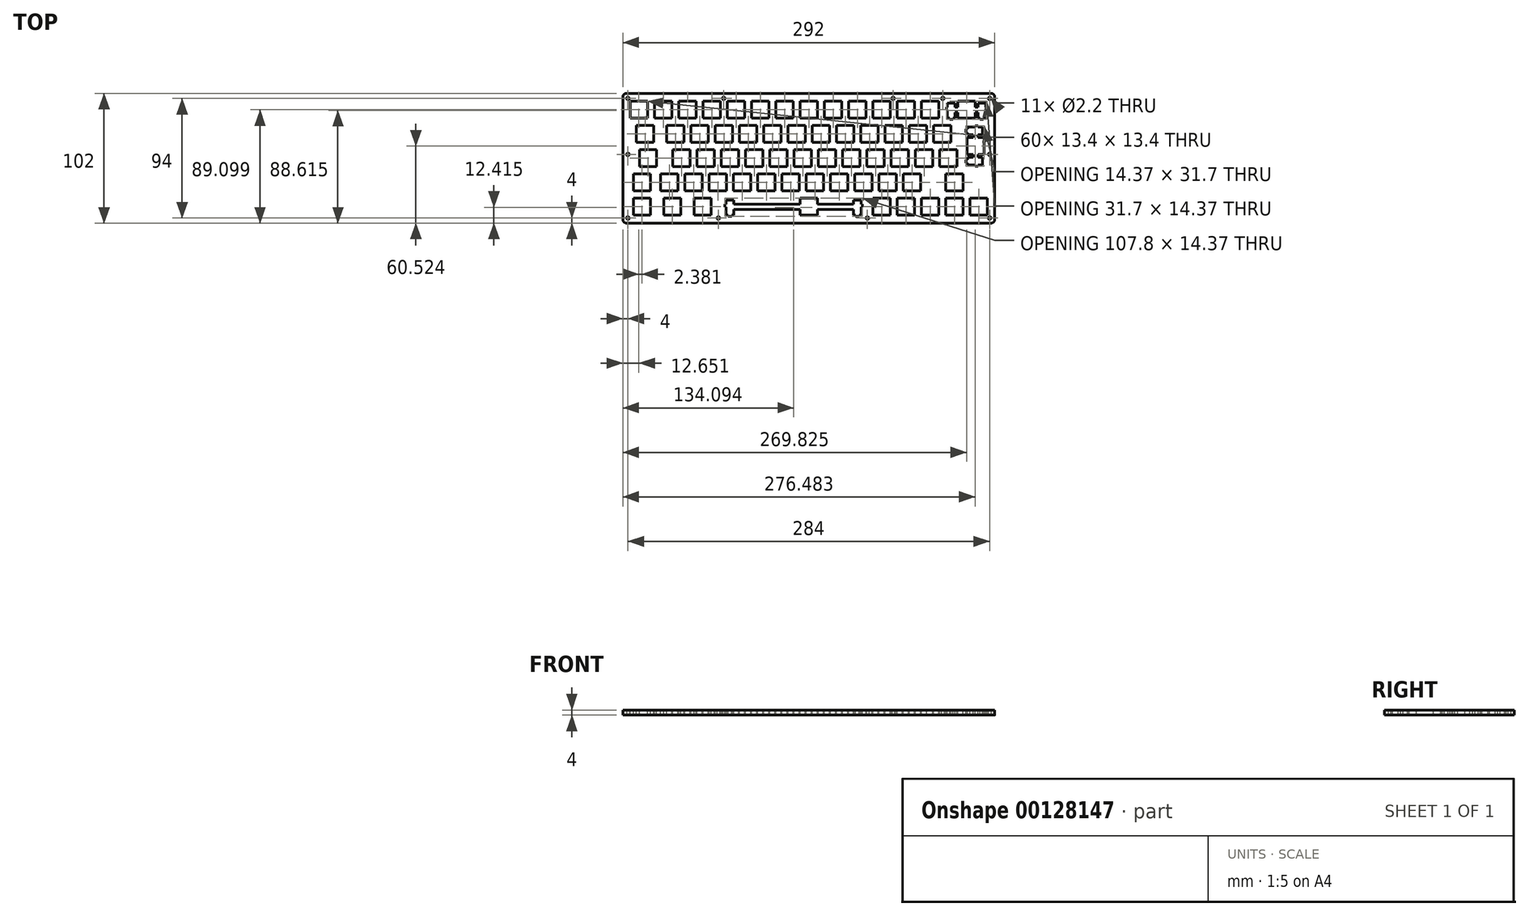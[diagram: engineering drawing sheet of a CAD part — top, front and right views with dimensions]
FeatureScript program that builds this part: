
annotation { "Feature Type Name" : "Feature", "Feature Type Description" : "" }
export const myFeature = defineFeature(function(context is Context, id is Id, definition is map)
    precondition{}
    {
        {
            var Q0;
            Q0=qCreatedBy(makeId("Top.planeOp"),FACE);
            var sketch = newSketch(context, id + "F0", { "sketchPlane" : qUnion([Q0])});
            skLineSegment(sketch, "E0.bottom", {"start": v(-143, 51) * mm, "end": v(143, 51) * mm});
            skLineSegment(sketch, "E0.top", {"start": v(-143, -51) * mm, "end": v(143, -51) * mm});
            skLineSegment(sketch, "E0.left", {"start": v(-146, 48) * mm, "end": v(-146, -48) * mm});
            skLineSegment(sketch, "E0.right", {"start": v(146, 48) * mm, "end": v(146, -48) * mm});
            skPoint(sketch, "E0.middle", {"position": v(0, 0) * mm});
            skPoint(sketch, "E1.visualSharp", {"position": v(-146, 51) * mm});
            skArc(sketch, "E1.filletArc", {"start": v(-143, 51) * mm, "mid": v(-145.12, 50.12) * mm, "end": v(-146, 48) * mm});
            skPoint(sketch, "E2.visualSharp", {"position": v(-146, -51) * mm});
            skArc(sketch, "E2.filletArc", {"start": v(-146, -48) * mm, "mid": v(-145.12, -50.12) * mm, "end": v(-143, -51) * mm});
            skPoint(sketch, "E3.visualSharp", {"position": v(146, 51) * mm});
            skArc(sketch, "E3.filletArc", {"start": v(146, 48) * mm, "mid": v(145.12, 50.12) * mm, "end": v(143, 51) * mm});
            skPoint(sketch, "E4.visualSharp", {"position": v(146, -51) * mm});
            skArc(sketch, "E4.filletArc", {"start": v(143, -51) * mm, "mid": v(145.12, -50.12) * mm, "end": v(146, -48) * mm});
            skCircle(sketch, "E5", {"center": v(-142, 47) * mm, "radius": 1.1 * mm});
            skCircle(sketch, "E6", {"center": v(-66.83, 47) * mm, "radius": 1.1 * mm});
            skCircle(sketch, "E7", {"center": v(66.17, 47) * mm, "radius": 1.1 * mm});
            skCircle(sketch, "E8", {"center": v(105.17, 47) * mm, "radius": 1.1 * mm});
            skCircle(sketch, "E9", {"center": v(142, 47) * mm, "radius": 1.1 * mm});
            skCircle(sketch, "E10", {"center": v(-142, -47) * mm, "radius": 1.1 * mm});
            skCircle(sketch, "E11", {"center": v(142, -47) * mm, "radius": 1.1 * mm});
            skCircle(sketch, "E12", {"center": v(-71, -47) * mm, "radius": 1.1 * mm});
            skCircle(sketch, "E13", {"center": v(46, -47) * mm, "radius": 1.1 * mm});
            skCircle(sketch, "E14", {"center": v(-142, 3) * mm, "radius": 1.1 * mm});
            skCircle(sketch, "E15", {"center": v(142, 3) * mm, "radius": 1.1 * mm});
            skSolve(sketch);
        }
        {
            var Q0;
            Q0=qSketchRegion(id+"F0",true);
            extrude(context, id + "F1", {"entities" : qUnion([Q0]), "depth" : 4 * mm});
        }
        {
            var Q0;
            Q0=makeQuery(id+"F1.opExtrude","CAP_FACE",FACE,{"disambiguationData":[OSD([sQuery(id+"F0.wireOp",EDGE,"E0.bottom"),sQuery(id+"F0.wireOp",EDGE,"E0.top"),sQuery(id+"F0.wireOp",EDGE,"E0.left"),sQuery(id+"F0.wireOp",EDGE,"E0.right"),sQuery(id+"F0.wireOp",EDGE,"E1.filletArc"),sQuery(id+"F0.wireOp",EDGE,"E2.filletArc"),sQuery(id+"F0.wireOp",EDGE,"E3.filletArc"),sQuery(id+"F0.wireOp",EDGE,"E4.filletArc"),sQuery(id+"F0.wireOp",EDGE,"E5"),sQuery(id+"F0.wireOp",EDGE,"E6"),sQuery(id+"F0.wireOp",EDGE,"E7"),sQuery(id+"F0.wireOp",EDGE,"E8"),sQuery(id+"F0.wireOp",EDGE,"E9"),sQuery(id+"F0.wireOp",EDGE,"E10"),sQuery(id+"F0.wireOp",EDGE,"E11"),sQuery(id+"F0.wireOp",EDGE,"E12"),sQuery(id+"F0.wireOp",EDGE,"E13"),sQuery(id+"F0.wireOp",EDGE,"E14"),sQuery(id+"F0.wireOp",EDGE,"E15")])],"isStart":false});
            var sketch = newSketch(context, id + "F2", { "sketchPlane" : qUnion([Q0])});
            skLineSegment(sketch, "E16", {"start": v(-18.6, -36.1) * mm, "end": v(-58.88, -36.1) * mm});
            skLineSegment(sketch, "E17", {"start": v(-58.88, -36.1) * mm, "end": v(-58.88, -32.87) * mm});
            skLineSegment(sketch, "E18", {"start": v(-58.88, -32.87) * mm, "end": v(-64.93, -32.87) * mm});
            skLineSegment(sketch, "E19", {"start": v(-64.93, -32.87) * mm, "end": v(-64.93, -36.1) * mm});
            skLineSegment(sketch, "E20", {"start": v(-64.93, -36.1) * mm, "end": v(-65.8, -36.1) * mm});
            skLineSegment(sketch, "E21", {"start": v(-65.8, -36.1) * mm, "end": v(-65.8, -38.3) * mm});
            skLineSegment(sketch, "E22", {"start": v(-65.8, -38.3) * mm, "end": v(-64.93, -38.3) * mm});
            skLineSegment(sketch, "E23", {"start": v(-64.93, -38.3) * mm, "end": v(-64.93, -44.57) * mm});
            skLineSegment(sketch, "E24", {"start": v(-64.93, -44.57) * mm, "end": v(-63.26, -44.57) * mm});
            skLineSegment(sketch, "E25", {"start": v(-63.26, -44.57) * mm, "end": v(-63.26, -45.77) * mm});
            skLineSegment(sketch, "E26", {"start": v(-63.26, -45.77) * mm, "end": v(-60.56, -45.77) * mm});
            skLineSegment(sketch, "E27", {"start": v(-60.56, -45.77) * mm, "end": v(-60.56, -44.57) * mm});
            skLineSegment(sketch, "E28", {"start": v(-60.56, -44.57) * mm, "end": v(-58.88, -44.57) * mm});
            skLineSegment(sketch, "E29", {"start": v(-58.88, -44.57) * mm, "end": v(-58.88, -40.1) * mm});
            skLineSegment(sketch, "E30", {"start": v(-58.88, -40.1) * mm, "end": v(-18.6, -40.1) * mm});
            skLineSegment(sketch, "E31", {"start": v(6.7, -40.1) * mm, "end": v(35.07, -40.1) * mm});
            skLineSegment(sketch, "E32", {"start": v(35.07, -40.1) * mm, "end": v(35.07, -44.57) * mm});
            skLineSegment(sketch, "E33", {"start": v(35.07, -44.57) * mm, "end": v(36.74, -44.57) * mm});
            skLineSegment(sketch, "E34", {"start": v(36.74, -44.57) * mm, "end": v(36.74, -45.77) * mm});
            skLineSegment(sketch, "E35", {"start": v(36.74, -45.77) * mm, "end": v(39.44, -45.77) * mm});
            skLineSegment(sketch, "E36", {"start": v(39.44, -45.77) * mm, "end": v(39.44, -44.57) * mm});
            skLineSegment(sketch, "E37", {"start": v(39.44, -44.57) * mm, "end": v(41.12, -44.57) * mm});
            skLineSegment(sketch, "E38", {"start": v(41.12, -44.57) * mm, "end": v(41.12, -38.3) * mm});
            skLineSegment(sketch, "E39", {"start": v(41.12, -38.3) * mm, "end": v(42, -38.3) * mm});
            skLineSegment(sketch, "E40", {"start": v(42, -38.3) * mm, "end": v(42, -36.1) * mm});
            skLineSegment(sketch, "E41", {"start": v(42, -36.1) * mm, "end": v(41.12, -36.1) * mm});
            skLineSegment(sketch, "E42", {"start": v(41.12, -36.1) * mm, "end": v(41.12, -32.87) * mm});
            skLineSegment(sketch, "E43", {"start": v(41.12, -32.87) * mm, "end": v(35.07, -32.87) * mm});
            skLineSegment(sketch, "E44", {"start": v(35.07, -32.87) * mm, "end": v(35.07, -36.1) * mm});
            skLineSegment(sketch, "E45", {"start": v(35.07, -36.1) * mm, "end": v(6.7, -36.1) * mm});
            skLineSegment(sketch, "E46", {"start": v(-137.67, -31.4) * mm, "end": v(-124.27, -31.4) * mm});
            skLineSegment(sketch, "E47", {"start": v(-124.27, -31.4) * mm, "end": v(-124.27, -44.8) * mm});
            skLineSegment(sketch, "E48", {"start": v(-124.27, -44.8) * mm, "end": v(-137.67, -44.8) * mm});
            skLineSegment(sketch, "E49", {"start": v(-137.67, -44.8) * mm, "end": v(-137.67, -31.4) * mm});
            skLineSegment(sketch, "E50", {"start": v(-113.86, -31.4) * mm, "end": v(-100.46, -31.4) * mm});
            skLineSegment(sketch, "E51", {"start": v(-100.46, -31.4) * mm, "end": v(-100.46, -44.8) * mm});
            skLineSegment(sketch, "E52", {"start": v(-100.46, -44.8) * mm, "end": v(-113.86, -44.8) * mm});
            skLineSegment(sketch, "E53", {"start": v(-113.86, -44.8) * mm, "end": v(-113.86, -31.4) * mm});
            skLineSegment(sketch, "E54", {"start": v(-90.04, -31.4) * mm, "end": v(-76.64, -31.4) * mm});
            skLineSegment(sketch, "E55", {"start": v(-76.64, -31.4) * mm, "end": v(-76.64, -44.8) * mm});
            skLineSegment(sketch, "E56", {"start": v(-76.64, -44.8) * mm, "end": v(-90.04, -44.8) * mm});
            skLineSegment(sketch, "E57", {"start": v(-90.04, -44.8) * mm, "end": v(-90.04, -31.4) * mm});
            skLineSegment(sketch, "E58", {"start": v(50.45, -31.4) * mm, "end": v(63.85, -31.4) * mm});
            skLineSegment(sketch, "E59", {"start": v(63.85, -31.4) * mm, "end": v(63.85, -44.8) * mm});
            skLineSegment(sketch, "E60", {"start": v(63.85, -44.8) * mm, "end": v(50.45, -44.8) * mm});
            skLineSegment(sketch, "E61", {"start": v(50.45, -44.8) * mm, "end": v(50.45, -31.4) * mm});
            skLineSegment(sketch, "E62", {"start": v(69.5, -31.4) * mm, "end": v(82.9, -31.4) * mm});
            skLineSegment(sketch, "E63", {"start": v(82.9, -31.4) * mm, "end": v(82.9, -44.8) * mm});
            skLineSegment(sketch, "E64", {"start": v(82.9, -44.8) * mm, "end": v(69.5, -44.8) * mm});
            skLineSegment(sketch, "E65", {"start": v(69.5, -44.8) * mm, "end": v(69.5, -31.4) * mm});
            skLineSegment(sketch, "E66", {"start": v(88.55, -31.4) * mm, "end": v(101.95, -31.4) * mm});
            skLineSegment(sketch, "E67", {"start": v(101.95, -31.4) * mm, "end": v(101.95, -44.8) * mm});
            skLineSegment(sketch, "E68", {"start": v(101.95, -44.8) * mm, "end": v(88.55, -44.8) * mm});
            skLineSegment(sketch, "E69", {"start": v(88.55, -44.8) * mm, "end": v(88.55, -31.4) * mm});
            skLineSegment(sketch, "E70", {"start": v(107.6, -31.4) * mm, "end": v(121, -31.4) * mm});
            skLineSegment(sketch, "E71", {"start": v(121, -31.4) * mm, "end": v(121, -44.8) * mm});
            skLineSegment(sketch, "E72", {"start": v(121, -44.8) * mm, "end": v(107.6, -44.8) * mm});
            skLineSegment(sketch, "E73", {"start": v(107.6, -44.8) * mm, "end": v(107.6, -31.4) * mm});
            skLineSegment(sketch, "E74", {"start": v(126.65, -31.4) * mm, "end": v(140.05, -31.4) * mm});
            skLineSegment(sketch, "E75", {"start": v(140.05, -31.4) * mm, "end": v(140.05, -44.8) * mm});
            skLineSegment(sketch, "E76", {"start": v(140.05, -44.8) * mm, "end": v(126.65, -44.8) * mm});
            skLineSegment(sketch, "E77", {"start": v(126.65, -44.8) * mm, "end": v(126.65, -31.4) * mm});
            skLineSegment(sketch, "E78", {"start": v(-137.67, -12.35) * mm, "end": v(-124.27, -12.35) * mm});
            skLineSegment(sketch, "E79", {"start": v(-124.27, -12.35) * mm, "end": v(-124.27, -25.75) * mm});
            skLineSegment(sketch, "E80", {"start": v(-124.27, -25.75) * mm, "end": v(-137.67, -25.75) * mm});
            skLineSegment(sketch, "E81", {"start": v(-137.67, -25.75) * mm, "end": v(-137.67, -12.35) * mm});
            skLineSegment(sketch, "E82", {"start": v(-116.24, -12.35) * mm, "end": v(-102.84, -12.35) * mm});
            skLineSegment(sketch, "E83", {"start": v(-102.84, -12.35) * mm, "end": v(-102.84, -25.75) * mm});
            skLineSegment(sketch, "E84", {"start": v(-102.84, -25.75) * mm, "end": v(-116.24, -25.75) * mm});
            skLineSegment(sketch, "E85", {"start": v(-116.24, -25.75) * mm, "end": v(-116.24, -12.35) * mm});
            skLineSegment(sketch, "E86", {"start": v(-97.19, -12.35) * mm, "end": v(-83.79, -12.35) * mm});
            skLineSegment(sketch, "E87", {"start": v(-83.79, -12.35) * mm, "end": v(-83.79, -25.75) * mm});
            skLineSegment(sketch, "E88", {"start": v(-83.79, -25.75) * mm, "end": v(-97.19, -25.75) * mm});
            skLineSegment(sketch, "E89", {"start": v(-97.19, -25.75) * mm, "end": v(-97.19, -12.35) * mm});
            skLineSegment(sketch, "E90", {"start": v(-78.14, -12.35) * mm, "end": v(-64.74, -12.35) * mm});
            skLineSegment(sketch, "E91", {"start": v(-64.74, -12.35) * mm, "end": v(-64.74, -25.75) * mm});
            skLineSegment(sketch, "E92", {"start": v(-64.74, -25.75) * mm, "end": v(-78.14, -25.75) * mm});
            skLineSegment(sketch, "E93", {"start": v(-78.14, -25.75) * mm, "end": v(-78.14, -12.35) * mm});
            skLineSegment(sketch, "E94", {"start": v(-59.09, -12.35) * mm, "end": v(-45.69, -12.35) * mm});
            skLineSegment(sketch, "E95", {"start": v(-45.69, -12.35) * mm, "end": v(-45.69, -25.75) * mm});
            skLineSegment(sketch, "E96", {"start": v(-45.69, -25.75) * mm, "end": v(-59.09, -25.75) * mm});
            skLineSegment(sketch, "E97", {"start": v(-59.09, -25.75) * mm, "end": v(-59.09, -12.35) * mm});
            skLineSegment(sketch, "E98", {"start": v(-40.04, -12.35) * mm, "end": v(-26.64, -12.35) * mm});
            skLineSegment(sketch, "E99", {"start": v(-26.64, -12.35) * mm, "end": v(-26.64, -25.75) * mm});
            skLineSegment(sketch, "E100", {"start": v(-26.64, -25.75) * mm, "end": v(-40.04, -25.75) * mm});
            skLineSegment(sketch, "E101", {"start": v(-40.04, -25.75) * mm, "end": v(-40.04, -12.35) * mm});
            skLineSegment(sketch, "E102", {"start": v(-20.99, -12.35) * mm, "end": v(-7.59, -12.35) * mm});
            skLineSegment(sketch, "E103", {"start": v(-7.59, -12.35) * mm, "end": v(-7.59, -25.75) * mm});
            skLineSegment(sketch, "E104", {"start": v(-7.59, -25.75) * mm, "end": v(-20.99, -25.75) * mm});
            skLineSegment(sketch, "E105", {"start": v(-20.99, -25.75) * mm, "end": v(-20.99, -12.35) * mm});
            skLineSegment(sketch, "E106", {"start": v(-1.94, -12.35) * mm, "end": v(11.46, -12.35) * mm});
            skLineSegment(sketch, "E107", {"start": v(11.46, -12.35) * mm, "end": v(11.46, -25.75) * mm});
            skLineSegment(sketch, "E108", {"start": v(11.46, -25.75) * mm, "end": v(-1.94, -25.75) * mm});
            skLineSegment(sketch, "E109", {"start": v(-1.94, -25.75) * mm, "end": v(-1.94, -12.35) * mm});
            skLineSegment(sketch, "E110", {"start": v(17.11, -12.35) * mm, "end": v(30.51, -12.35) * mm});
            skLineSegment(sketch, "E111", {"start": v(30.51, -12.35) * mm, "end": v(30.51, -25.75) * mm});
            skLineSegment(sketch, "E112", {"start": v(30.51, -25.75) * mm, "end": v(17.11, -25.75) * mm});
            skLineSegment(sketch, "E113", {"start": v(17.11, -25.75) * mm, "end": v(17.11, -12.35) * mm});
            skLineSegment(sketch, "E114", {"start": v(36.16, -12.35) * mm, "end": v(49.56, -12.35) * mm});
            skLineSegment(sketch, "E115", {"start": v(49.56, -12.35) * mm, "end": v(49.56, -25.75) * mm});
            skLineSegment(sketch, "E116", {"start": v(49.56, -25.75) * mm, "end": v(36.16, -25.75) * mm});
            skLineSegment(sketch, "E117", {"start": v(36.16, -25.75) * mm, "end": v(36.16, -12.35) * mm});
            skLineSegment(sketch, "E118", {"start": v(55.21, -12.35) * mm, "end": v(68.61, -12.35) * mm});
            skLineSegment(sketch, "E119", {"start": v(68.61, -12.35) * mm, "end": v(68.61, -25.75) * mm});
            skLineSegment(sketch, "E120", {"start": v(68.61, -25.75) * mm, "end": v(55.21, -25.75) * mm});
            skLineSegment(sketch, "E121", {"start": v(55.21, -25.75) * mm, "end": v(55.21, -12.35) * mm});
            skLineSegment(sketch, "E122", {"start": v(74.26, -12.35) * mm, "end": v(87.66, -12.35) * mm});
            skLineSegment(sketch, "E123", {"start": v(87.66, -12.35) * mm, "end": v(87.66, -25.75) * mm});
            skLineSegment(sketch, "E124", {"start": v(87.66, -25.75) * mm, "end": v(74.26, -25.75) * mm});
            skLineSegment(sketch, "E125", {"start": v(74.26, -25.75) * mm, "end": v(74.26, -12.35) * mm});
            skLineSegment(sketch, "E126", {"start": v(107.6, -12.35) * mm, "end": v(121, -12.35) * mm});
            skLineSegment(sketch, "E127", {"start": v(121, -12.35) * mm, "end": v(121, -25.75) * mm});
            skLineSegment(sketch, "E128", {"start": v(121, -25.75) * mm, "end": v(107.6, -25.75) * mm});
            skLineSegment(sketch, "E129", {"start": v(107.6, -25.75) * mm, "end": v(107.6, -12.35) * mm});
            skLineSegment(sketch, "E130", {"start": v(-132.9, 6.7) * mm, "end": v(-119.5, 6.7) * mm});
            skLineSegment(sketch, "E131", {"start": v(-119.5, 6.7) * mm, "end": v(-119.5, -6.7) * mm});
            skLineSegment(sketch, "E132", {"start": v(-119.5, -6.7) * mm, "end": v(-132.9, -6.7) * mm});
            skLineSegment(sketch, "E133", {"start": v(-132.9, -6.7) * mm, "end": v(-132.9, 6.7) * mm});
            skLineSegment(sketch, "E134", {"start": v(-106.71, 6.7) * mm, "end": v(-93.31, 6.7) * mm});
            skLineSegment(sketch, "E135", {"start": v(-93.31, 6.7) * mm, "end": v(-93.31, -6.7) * mm});
            skLineSegment(sketch, "E136", {"start": v(-93.31, -6.7) * mm, "end": v(-106.71, -6.7) * mm});
            skLineSegment(sketch, "E137", {"start": v(-106.71, -6.7) * mm, "end": v(-106.71, 6.7) * mm});
            skLineSegment(sketch, "E138", {"start": v(-87.66, 6.7) * mm, "end": v(-74.26, 6.7) * mm});
            skLineSegment(sketch, "E139", {"start": v(-74.26, 6.7) * mm, "end": v(-74.26, -6.7) * mm});
            skLineSegment(sketch, "E140", {"start": v(-74.26, -6.7) * mm, "end": v(-87.66, -6.7) * mm});
            skLineSegment(sketch, "E141", {"start": v(-87.66, -6.7) * mm, "end": v(-87.66, 6.7) * mm});
            skLineSegment(sketch, "E142", {"start": v(-68.61, 6.7) * mm, "end": v(-55.21, 6.7) * mm});
            skLineSegment(sketch, "E143", {"start": v(-55.21, 6.7) * mm, "end": v(-55.21, -6.7) * mm});
            skLineSegment(sketch, "E144", {"start": v(-55.21, -6.7) * mm, "end": v(-68.61, -6.7) * mm});
            skLineSegment(sketch, "E145", {"start": v(-68.61, -6.7) * mm, "end": v(-68.61, 6.7) * mm});
            skLineSegment(sketch, "E146", {"start": v(-49.56, 6.7) * mm, "end": v(-36.16, 6.7) * mm});
            skLineSegment(sketch, "E147", {"start": v(-36.16, 6.7) * mm, "end": v(-36.16, -6.7) * mm});
            skLineSegment(sketch, "E148", {"start": v(-36.16, -6.7) * mm, "end": v(-49.56, -6.7) * mm});
            skLineSegment(sketch, "E149", {"start": v(-49.56, -6.7) * mm, "end": v(-49.56, 6.7) * mm});
            skLineSegment(sketch, "E150", {"start": v(-30.51, 6.7) * mm, "end": v(-17.11, 6.7) * mm});
            skLineSegment(sketch, "E151", {"start": v(-17.11, 6.7) * mm, "end": v(-17.11, -6.7) * mm});
            skLineSegment(sketch, "E152", {"start": v(-17.11, -6.7) * mm, "end": v(-30.51, -6.7) * mm});
            skLineSegment(sketch, "E153", {"start": v(-30.51, -6.7) * mm, "end": v(-30.51, 6.7) * mm});
            skLineSegment(sketch, "E154", {"start": v(-11.46, 6.7) * mm, "end": v(1.94, 6.7) * mm});
            skLineSegment(sketch, "E155", {"start": v(1.94, 6.7) * mm, "end": v(1.94, -6.7) * mm});
            skLineSegment(sketch, "E156", {"start": v(1.94, -6.7) * mm, "end": v(-11.46, -6.7) * mm});
            skLineSegment(sketch, "E157", {"start": v(-11.46, -6.7) * mm, "end": v(-11.46, 6.7) * mm});
            skLineSegment(sketch, "E158", {"start": v(7.59, 6.7) * mm, "end": v(20.99, 6.7) * mm});
            skLineSegment(sketch, "E159", {"start": v(20.99, 6.7) * mm, "end": v(20.99, -6.7) * mm});
            skLineSegment(sketch, "E160", {"start": v(20.99, -6.7) * mm, "end": v(7.59, -6.7) * mm});
            skLineSegment(sketch, "E161", {"start": v(7.59, -6.7) * mm, "end": v(7.59, 6.7) * mm});
            skLineSegment(sketch, "E162", {"start": v(26.64, 6.7) * mm, "end": v(40.04, 6.7) * mm});
            skLineSegment(sketch, "E163", {"start": v(40.04, 6.7) * mm, "end": v(40.04, -6.7) * mm});
            skLineSegment(sketch, "E164", {"start": v(40.04, -6.7) * mm, "end": v(26.64, -6.7) * mm});
            skLineSegment(sketch, "E165", {"start": v(26.64, -6.7) * mm, "end": v(26.64, 6.7) * mm});
            skLineSegment(sketch, "E166", {"start": v(45.69, 6.7) * mm, "end": v(59.09, 6.7) * mm});
            skLineSegment(sketch, "E167", {"start": v(59.09, 6.7) * mm, "end": v(59.09, -6.7) * mm});
            skLineSegment(sketch, "E168", {"start": v(59.09, -6.7) * mm, "end": v(45.69, -6.7) * mm});
            skLineSegment(sketch, "E169", {"start": v(45.69, -6.7) * mm, "end": v(45.69, 6.7) * mm});
            skLineSegment(sketch, "E170", {"start": v(64.74, 6.7) * mm, "end": v(78.14, 6.7) * mm});
            skLineSegment(sketch, "E171", {"start": v(78.14, 6.7) * mm, "end": v(78.14, -6.7) * mm});
            skLineSegment(sketch, "E172", {"start": v(78.14, -6.7) * mm, "end": v(64.74, -6.7) * mm});
            skLineSegment(sketch, "E173", {"start": v(64.74, -6.7) * mm, "end": v(64.74, 6.7) * mm});
            skLineSegment(sketch, "E174", {"start": v(83.79, 6.7) * mm, "end": v(97.19, 6.7) * mm});
            skLineSegment(sketch, "E175", {"start": v(97.19, 6.7) * mm, "end": v(97.19, -6.7) * mm});
            skLineSegment(sketch, "E176", {"start": v(97.19, -6.7) * mm, "end": v(83.79, -6.7) * mm});
            skLineSegment(sketch, "E177", {"start": v(83.79, -6.7) * mm, "end": v(83.79, 6.7) * mm});
            skLineSegment(sketch, "E178", {"start": v(102.84, 6.7) * mm, "end": v(116.24, 6.7) * mm});
            skLineSegment(sketch, "E179", {"start": v(116.24, 6.7) * mm, "end": v(116.24, -6.7) * mm});
            skLineSegment(sketch, "E180", {"start": v(116.24, -6.7) * mm, "end": v(102.84, -6.7) * mm});
            skLineSegment(sketch, "E181", {"start": v(102.84, -6.7) * mm, "end": v(102.84, 6.7) * mm});
            skLineSegment(sketch, "E182", {"start": v(130.77, 25.37) * mm, "end": v(130.77, 24.5) * mm});
            skLineSegment(sketch, "E183", {"start": v(130.77, 24.5) * mm, "end": v(124.5, 24.5) * mm});
            skLineSegment(sketch, "E184", {"start": v(124.5, 24.5) * mm, "end": v(124.5, 22.83) * mm});
            skLineSegment(sketch, "E185", {"start": v(124.5, 22.83) * mm, "end": v(123.3, 22.83) * mm});
            skLineSegment(sketch, "E186", {"start": v(123.3, 22.83) * mm, "end": v(123.3, 20.12) * mm});
            skLineSegment(sketch, "E187", {"start": v(123.3, 20.12) * mm, "end": v(124.5, 20.12) * mm});
            skLineSegment(sketch, "E188", {"start": v(124.5, 20.12) * mm, "end": v(124.5, 18.45) * mm});
            skLineSegment(sketch, "E189", {"start": v(124.5, 18.45) * mm, "end": v(128.97, 18.45) * mm});
            skLineSegment(sketch, "E190", {"start": v(128.97, 18.45) * mm, "end": v(128.97, 16.23) * mm});
            skLineSegment(sketch, "E191", {"start": v(128.97, 16.23) * mm, "end": v(124.27, 16.23) * mm});
            skLineSegment(sketch, "E192", {"start": v(124.27, 16.23) * mm, "end": v(124.27, 2.82) * mm});
            skLineSegment(sketch, "E193", {"start": v(124.27, 2.82) * mm, "end": v(128.97, 2.82) * mm});
            skLineSegment(sketch, "E194", {"start": v(128.97, 2.82) * mm, "end": v(128.97, 0.6) * mm});
            skLineSegment(sketch, "E195", {"start": v(128.97, 0.6) * mm, "end": v(124.5, 0.6) * mm});
            skLineSegment(sketch, "E196", {"start": v(124.5, 0.6) * mm, "end": v(124.5, -1.08) * mm});
            skLineSegment(sketch, "E197", {"start": v(124.5, -1.08) * mm, "end": v(123.3, -1.08) * mm});
            skLineSegment(sketch, "E198", {"start": v(123.3, -1.08) * mm, "end": v(123.3, -3.77) * mm});
            skLineSegment(sketch, "E199", {"start": v(123.3, -3.77) * mm, "end": v(124.5, -3.77) * mm});
            skLineSegment(sketch, "E200", {"start": v(124.5, -3.77) * mm, "end": v(124.5, -5.45) * mm});
            skLineSegment(sketch, "E201", {"start": v(124.5, -5.45) * mm, "end": v(130.77, -5.45) * mm});
            skLineSegment(sketch, "E202", {"start": v(130.77, -5.45) * mm, "end": v(130.77, -6.33) * mm});
            skLineSegment(sketch, "E203", {"start": v(130.77, -6.33) * mm, "end": v(132.97, -6.33) * mm});
            skLineSegment(sketch, "E204", {"start": v(132.97, -6.33) * mm, "end": v(132.97, -5.45) * mm});
            skLineSegment(sketch, "E205", {"start": v(132.97, -5.45) * mm, "end": v(136.2, -5.45) * mm});
            skLineSegment(sketch, "E206", {"start": v(136.2, -5.45) * mm, "end": v(136.2, 0.6) * mm});
            skLineSegment(sketch, "E207", {"start": v(136.2, 0.6) * mm, "end": v(132.97, 0.6) * mm});
            skLineSegment(sketch, "E208", {"start": v(132.97, 0.6) * mm, "end": v(132.97, 2.82) * mm});
            skLineSegment(sketch, "E209", {"start": v(132.97, 2.82) * mm, "end": v(137.67, 2.82) * mm});
            skLineSegment(sketch, "E210", {"start": v(137.67, 2.82) * mm, "end": v(137.67, 16.23) * mm});
            skLineSegment(sketch, "E211", {"start": v(137.67, 16.23) * mm, "end": v(132.97, 16.23) * mm});
            skLineSegment(sketch, "E212", {"start": v(132.97, 16.23) * mm, "end": v(132.97, 18.45) * mm});
            skLineSegment(sketch, "E213", {"start": v(132.97, 18.45) * mm, "end": v(136.2, 18.45) * mm});
            skLineSegment(sketch, "E214", {"start": v(136.2, 18.45) * mm, "end": v(136.2, 24.5) * mm});
            skLineSegment(sketch, "E215", {"start": v(136.2, 24.5) * mm, "end": v(132.97, 24.5) * mm});
            skLineSegment(sketch, "E216", {"start": v(132.97, 24.5) * mm, "end": v(132.97, 25.37) * mm});
            skLineSegment(sketch, "E217", {"start": v(132.97, 25.37) * mm, "end": v(130.77, 25.37) * mm});
            skLineSegment(sketch, "E218", {"start": v(-135.29, 25.75) * mm, "end": v(-121.89, 25.75) * mm});
            skLineSegment(sketch, "E219", {"start": v(-121.89, 25.75) * mm, "end": v(-121.89, 12.35) * mm});
            skLineSegment(sketch, "E220", {"start": v(-121.89, 12.35) * mm, "end": v(-135.29, 12.35) * mm});
            skLineSegment(sketch, "E221", {"start": v(-135.29, 12.35) * mm, "end": v(-135.29, 25.75) * mm});
            skLineSegment(sketch, "E222", {"start": v(-111.47, 25.75) * mm, "end": v(-98.07, 25.75) * mm});
            skLineSegment(sketch, "E223", {"start": v(-98.07, 25.75) * mm, "end": v(-98.07, 12.35) * mm});
            skLineSegment(sketch, "E224", {"start": v(-98.07, 12.35) * mm, "end": v(-111.47, 12.35) * mm});
            skLineSegment(sketch, "E225", {"start": v(-111.47, 12.35) * mm, "end": v(-111.47, 25.75) * mm});
            skLineSegment(sketch, "E226", {"start": v(-92.42, 25.75) * mm, "end": v(-79.02, 25.75) * mm});
            skLineSegment(sketch, "E227", {"start": v(-79.02, 25.75) * mm, "end": v(-79.02, 12.35) * mm});
            skLineSegment(sketch, "E228", {"start": v(-79.02, 12.35) * mm, "end": v(-92.42, 12.35) * mm});
            skLineSegment(sketch, "E229", {"start": v(-92.42, 12.35) * mm, "end": v(-92.42, 25.75) * mm});
            skLineSegment(sketch, "E230", {"start": v(-73.37, 25.75) * mm, "end": v(-59.97, 25.75) * mm});
            skLineSegment(sketch, "E231", {"start": v(-59.97, 25.75) * mm, "end": v(-59.97, 12.35) * mm});
            skLineSegment(sketch, "E232", {"start": v(-59.97, 12.35) * mm, "end": v(-73.37, 12.35) * mm});
            skLineSegment(sketch, "E233", {"start": v(-73.37, 12.35) * mm, "end": v(-73.37, 25.75) * mm});
            skLineSegment(sketch, "E234", {"start": v(-54.32, 25.75) * mm, "end": v(-40.92, 25.75) * mm});
            skLineSegment(sketch, "E235", {"start": v(-40.92, 25.75) * mm, "end": v(-40.92, 12.35) * mm});
            skLineSegment(sketch, "E236", {"start": v(-40.92, 12.35) * mm, "end": v(-54.32, 12.35) * mm});
            skLineSegment(sketch, "E237", {"start": v(-54.32, 12.35) * mm, "end": v(-54.32, 25.75) * mm});
            skLineSegment(sketch, "E238", {"start": v(-35.28, 25.75) * mm, "end": v(-21.87, 25.75) * mm});
            skLineSegment(sketch, "E239", {"start": v(-21.87, 25.75) * mm, "end": v(-21.87, 12.35) * mm});
            skLineSegment(sketch, "E240", {"start": v(-21.87, 12.35) * mm, "end": v(-35.28, 12.35) * mm});
            skLineSegment(sketch, "E241", {"start": v(-35.28, 12.35) * mm, "end": v(-35.28, 25.75) * mm});
            skLineSegment(sketch, "E242", {"start": v(-16.22, 25.75) * mm, "end": v(-2.82, 25.75) * mm});
            skLineSegment(sketch, "E243", {"start": v(-2.82, 25.75) * mm, "end": v(-2.82, 12.35) * mm});
            skLineSegment(sketch, "E244", {"start": v(-2.82, 12.35) * mm, "end": v(-16.22, 12.35) * mm});
            skLineSegment(sketch, "E245", {"start": v(-16.22, 12.35) * mm, "end": v(-16.22, 25.75) * mm});
            skLineSegment(sketch, "E246", {"start": v(2.83, 25.75) * mm, "end": v(16.23, 25.75) * mm});
            skLineSegment(sketch, "E247", {"start": v(16.23, 25.75) * mm, "end": v(16.23, 12.35) * mm});
            skLineSegment(sketch, "E248", {"start": v(16.23, 12.35) * mm, "end": v(2.83, 12.35) * mm});
            skLineSegment(sketch, "E249", {"start": v(2.83, 12.35) * mm, "end": v(2.83, 25.75) * mm});
            skLineSegment(sketch, "E250", {"start": v(21.88, 25.75) * mm, "end": v(35.28, 25.75) * mm});
            skLineSegment(sketch, "E251", {"start": v(35.28, 25.75) * mm, "end": v(35.28, 12.35) * mm});
            skLineSegment(sketch, "E252", {"start": v(35.28, 12.35) * mm, "end": v(21.88, 12.35) * mm});
            skLineSegment(sketch, "E253", {"start": v(21.88, 12.35) * mm, "end": v(21.88, 25.75) * mm});
            skLineSegment(sketch, "E254", {"start": v(40.93, 25.75) * mm, "end": v(54.33, 25.75) * mm});
            skLineSegment(sketch, "E255", {"start": v(54.33, 25.75) * mm, "end": v(54.33, 12.35) * mm});
            skLineSegment(sketch, "E256", {"start": v(54.33, 12.35) * mm, "end": v(40.93, 12.35) * mm});
            skLineSegment(sketch, "E257", {"start": v(40.93, 12.35) * mm, "end": v(40.93, 25.75) * mm});
            skLineSegment(sketch, "E258", {"start": v(59.98, 25.75) * mm, "end": v(73.38, 25.75) * mm});
            skLineSegment(sketch, "E259", {"start": v(73.38, 25.75) * mm, "end": v(73.38, 12.35) * mm});
            skLineSegment(sketch, "E260", {"start": v(73.38, 12.35) * mm, "end": v(59.98, 12.35) * mm});
            skLineSegment(sketch, "E261", {"start": v(59.98, 12.35) * mm, "end": v(59.98, 25.75) * mm});
            skLineSegment(sketch, "E262", {"start": v(79.03, 25.75) * mm, "end": v(92.43, 25.75) * mm});
            skLineSegment(sketch, "E263", {"start": v(92.43, 25.75) * mm, "end": v(92.43, 12.35) * mm});
            skLineSegment(sketch, "E264", {"start": v(92.43, 12.35) * mm, "end": v(79.03, 12.35) * mm});
            skLineSegment(sketch, "E265", {"start": v(79.03, 12.35) * mm, "end": v(79.03, 25.75) * mm});
            skLineSegment(sketch, "E266", {"start": v(98.08, 25.75) * mm, "end": v(111.47, 25.75) * mm});
            skLineSegment(sketch, "E267", {"start": v(111.47, 25.75) * mm, "end": v(111.47, 12.35) * mm});
            skLineSegment(sketch, "E268", {"start": v(111.47, 12.35) * mm, "end": v(98.08, 12.35) * mm});
            skLineSegment(sketch, "E269", {"start": v(98.08, 12.35) * mm, "end": v(98.08, 25.75) * mm});
            skLineSegment(sketch, "E270", {"start": v(117.13, 44.8) * mm, "end": v(117.13, 40.1) * mm});
            skLineSegment(sketch, "E271", {"start": v(117.13, 40.1) * mm, "end": v(114.9, 40.1) * mm});
            skLineSegment(sketch, "E272", {"start": v(114.9, 40.1) * mm, "end": v(114.9, 43.33) * mm});
            skLineSegment(sketch, "E273", {"start": v(114.9, 43.33) * mm, "end": v(108.85, 43.33) * mm});
            skLineSegment(sketch, "E274", {"start": v(108.85, 43.33) * mm, "end": v(108.85, 40.1) * mm});
            skLineSegment(sketch, "E275", {"start": v(108.85, 40.1) * mm, "end": v(107.97, 40.1) * mm});
            skLineSegment(sketch, "E276", {"start": v(107.97, 40.1) * mm, "end": v(107.97, 37.9) * mm});
            skLineSegment(sketch, "E277", {"start": v(107.97, 37.9) * mm, "end": v(108.85, 37.9) * mm});
            skLineSegment(sketch, "E278", {"start": v(108.85, 37.9) * mm, "end": v(108.85, 31.63) * mm});
            skLineSegment(sketch, "E279", {"start": v(108.85, 31.63) * mm, "end": v(110.52, 31.63) * mm});
            skLineSegment(sketch, "E280", {"start": v(110.52, 31.63) * mm, "end": v(110.52, 30.43) * mm});
            skLineSegment(sketch, "E281", {"start": v(110.52, 30.43) * mm, "end": v(113.22, 30.43) * mm});
            skLineSegment(sketch, "E282", {"start": v(113.22, 30.43) * mm, "end": v(113.22, 31.63) * mm});
            skLineSegment(sketch, "E283", {"start": v(113.22, 31.63) * mm, "end": v(114.9, 31.63) * mm});
            skLineSegment(sketch, "E284", {"start": v(114.9, 31.63) * mm, "end": v(114.9, 36.1) * mm});
            skLineSegment(sketch, "E285", {"start": v(114.9, 36.1) * mm, "end": v(117.13, 36.1) * mm});
            skLineSegment(sketch, "E286", {"start": v(117.13, 36.1) * mm, "end": v(117.13, 31.4) * mm});
            skLineSegment(sketch, "E287", {"start": v(117.13, 31.4) * mm, "end": v(130.53, 31.4) * mm});
            skLineSegment(sketch, "E288", {"start": v(130.53, 31.4) * mm, "end": v(130.53, 36.1) * mm});
            skLineSegment(sketch, "E289", {"start": v(130.53, 36.1) * mm, "end": v(132.75, 36.1) * mm});
            skLineSegment(sketch, "E290", {"start": v(132.75, 36.1) * mm, "end": v(132.75, 31.63) * mm});
            skLineSegment(sketch, "E291", {"start": v(132.75, 31.63) * mm, "end": v(134.43, 31.63) * mm});
            skLineSegment(sketch, "E292", {"start": v(134.43, 31.63) * mm, "end": v(134.43, 30.43) * mm});
            skLineSegment(sketch, "E293", {"start": v(134.43, 30.43) * mm, "end": v(137.12, 30.43) * mm});
            skLineSegment(sketch, "E294", {"start": v(137.12, 30.43) * mm, "end": v(137.12, 31.63) * mm});
            skLineSegment(sketch, "E295", {"start": v(137.12, 31.63) * mm, "end": v(138.8, 31.63) * mm});
            skLineSegment(sketch, "E296", {"start": v(138.8, 31.63) * mm, "end": v(138.8, 37.9) * mm});
            skLineSegment(sketch, "E297", {"start": v(138.8, 37.9) * mm, "end": v(139.68, 37.9) * mm});
            skLineSegment(sketch, "E298", {"start": v(139.68, 37.9) * mm, "end": v(139.68, 40.1) * mm});
            skLineSegment(sketch, "E299", {"start": v(139.68, 40.1) * mm, "end": v(138.8, 40.1) * mm});
            skLineSegment(sketch, "E300", {"start": v(138.8, 40.1) * mm, "end": v(138.8, 43.33) * mm});
            skLineSegment(sketch, "E301", {"start": v(138.8, 43.33) * mm, "end": v(132.75, 43.33) * mm});
            skLineSegment(sketch, "E302", {"start": v(132.75, 43.33) * mm, "end": v(132.75, 40.1) * mm});
            skLineSegment(sketch, "E303", {"start": v(132.75, 40.1) * mm, "end": v(130.53, 40.1) * mm});
            skLineSegment(sketch, "E304", {"start": v(130.53, 40.1) * mm, "end": v(130.53, 44.8) * mm});
            skLineSegment(sketch, "E305", {"start": v(130.53, 44.8) * mm, "end": v(117.13, 44.8) * mm});
            skLineSegment(sketch, "E306", {"start": v(-140.05, 44.8) * mm, "end": v(-126.65, 44.8) * mm});
            skLineSegment(sketch, "E307", {"start": v(-126.65, 44.8) * mm, "end": v(-126.65, 31.4) * mm});
            skLineSegment(sketch, "E308", {"start": v(-126.65, 31.4) * mm, "end": v(-140.05, 31.4) * mm});
            skLineSegment(sketch, "E309", {"start": v(-140.05, 31.4) * mm, "end": v(-140.05, 44.8) * mm});
            skLineSegment(sketch, "E310", {"start": v(-121, 44.8) * mm, "end": v(-107.6, 44.8) * mm});
            skLineSegment(sketch, "E311", {"start": v(-107.6, 44.8) * mm, "end": v(-107.6, 31.4) * mm});
            skLineSegment(sketch, "E312", {"start": v(-107.6, 31.4) * mm, "end": v(-121, 31.4) * mm});
            skLineSegment(sketch, "E313", {"start": v(-121, 31.4) * mm, "end": v(-121, 44.8) * mm});
            skLineSegment(sketch, "E314", {"start": v(-101.95, 44.8) * mm, "end": v(-88.55, 44.8) * mm});
            skLineSegment(sketch, "E315", {"start": v(-88.55, 44.8) * mm, "end": v(-88.55, 31.4) * mm});
            skLineSegment(sketch, "E316", {"start": v(-88.55, 31.4) * mm, "end": v(-101.95, 31.4) * mm});
            skLineSegment(sketch, "E317", {"start": v(-101.95, 31.4) * mm, "end": v(-101.95, 44.8) * mm});
            skLineSegment(sketch, "E318", {"start": v(-82.9, 44.8) * mm, "end": v(-69.5, 44.8) * mm});
            skLineSegment(sketch, "E319", {"start": v(-69.5, 44.8) * mm, "end": v(-69.5, 31.4) * mm});
            skLineSegment(sketch, "E320", {"start": v(-69.5, 31.4) * mm, "end": v(-82.9, 31.4) * mm});
            skLineSegment(sketch, "E321", {"start": v(-82.9, 31.4) * mm, "end": v(-82.9, 44.8) * mm});
            skLineSegment(sketch, "E322", {"start": v(-63.85, 44.8) * mm, "end": v(-50.45, 44.8) * mm});
            skLineSegment(sketch, "E323", {"start": v(-50.45, 44.8) * mm, "end": v(-50.45, 31.4) * mm});
            skLineSegment(sketch, "E324", {"start": v(-50.45, 31.4) * mm, "end": v(-63.85, 31.4) * mm});
            skLineSegment(sketch, "E325", {"start": v(-63.85, 31.4) * mm, "end": v(-63.85, 44.8) * mm});
            skLineSegment(sketch, "E326", {"start": v(-44.8, 44.8) * mm, "end": v(-31.4, 44.8) * mm});
            skLineSegment(sketch, "E327", {"start": v(-31.4, 44.8) * mm, "end": v(-31.4, 31.4) * mm});
            skLineSegment(sketch, "E328", {"start": v(-31.4, 31.4) * mm, "end": v(-44.8, 31.4) * mm});
            skLineSegment(sketch, "E329", {"start": v(-44.8, 31.4) * mm, "end": v(-44.8, 44.8) * mm});
            skLineSegment(sketch, "E330", {"start": v(-25.75, 44.8) * mm, "end": v(-12.35, 44.8) * mm});
            skLineSegment(sketch, "E331", {"start": v(-12.35, 44.8) * mm, "end": v(-12.35, 31.4) * mm});
            skLineSegment(sketch, "E332", {"start": v(-12.35, 31.4) * mm, "end": v(-25.75, 31.4) * mm});
            skLineSegment(sketch, "E333", {"start": v(-25.75, 31.4) * mm, "end": v(-25.75, 44.8) * mm});
            skLineSegment(sketch, "E334", {"start": v(-6.7, 44.8) * mm, "end": v(6.7, 44.8) * mm});
            skLineSegment(sketch, "E335", {"start": v(6.7, 44.8) * mm, "end": v(6.7, 31.4) * mm});
            skLineSegment(sketch, "E336", {"start": v(6.7, 31.4) * mm, "end": v(-6.7, 31.4) * mm});
            skLineSegment(sketch, "E337", {"start": v(-6.7, 31.4) * mm, "end": v(-6.7, 44.8) * mm});
            skLineSegment(sketch, "E338", {"start": v(12.35, 44.8) * mm, "end": v(25.75, 44.8) * mm});
            skLineSegment(sketch, "E339", {"start": v(25.75, 44.8) * mm, "end": v(25.75, 31.4) * mm});
            skLineSegment(sketch, "E340", {"start": v(25.75, 31.4) * mm, "end": v(12.35, 31.4) * mm});
            skLineSegment(sketch, "E341", {"start": v(12.35, 31.4) * mm, "end": v(12.35, 44.8) * mm});
            skLineSegment(sketch, "E342", {"start": v(31.4, 44.8) * mm, "end": v(44.8, 44.8) * mm});
            skLineSegment(sketch, "E343", {"start": v(44.8, 44.8) * mm, "end": v(44.8, 31.4) * mm});
            skLineSegment(sketch, "E344", {"start": v(44.8, 31.4) * mm, "end": v(31.4, 31.4) * mm});
            skLineSegment(sketch, "E345", {"start": v(31.4, 31.4) * mm, "end": v(31.4, 44.8) * mm});
            skLineSegment(sketch, "E346", {"start": v(50.45, 44.8) * mm, "end": v(63.85, 44.8) * mm});
            skLineSegment(sketch, "E347", {"start": v(63.85, 44.8) * mm, "end": v(63.85, 31.4) * mm});
            skLineSegment(sketch, "E348", {"start": v(63.85, 31.4) * mm, "end": v(50.45, 31.4) * mm});
            skLineSegment(sketch, "E349", {"start": v(50.45, 31.4) * mm, "end": v(50.45, 44.8) * mm});
            skLineSegment(sketch, "E350", {"start": v(69.5, 44.8) * mm, "end": v(82.9, 44.8) * mm});
            skLineSegment(sketch, "E351", {"start": v(82.9, 44.8) * mm, "end": v(82.9, 31.4) * mm});
            skLineSegment(sketch, "E352", {"start": v(82.9, 31.4) * mm, "end": v(69.5, 31.4) * mm});
            skLineSegment(sketch, "E353", {"start": v(69.5, 31.4) * mm, "end": v(69.5, 44.8) * mm});
            skLineSegment(sketch, "E354", {"start": v(88.55, 44.8) * mm, "end": v(101.95, 44.8) * mm});
            skLineSegment(sketch, "E355", {"start": v(101.95, 44.8) * mm, "end": v(101.95, 31.4) * mm});
            skLineSegment(sketch, "E356", {"start": v(101.95, 31.4) * mm, "end": v(88.55, 31.4) * mm});
            skLineSegment(sketch, "E357", {"start": v(88.55, 31.4) * mm, "end": v(88.55, 44.8) * mm});
            skPoint(sketch, "E358.middle", {"position": v(0, -38.1) * mm});
            skLineSegment(sketch, "E359", {"start": v(-18.6, -36.1) * mm, "end": v(-6.7, -36.1) * mm});
            skLineSegment(sketch, "E360", {"start": v(-18.6, -40.1) * mm, "end": v(-6.7, -40.1) * mm});
            skLineSegment(sketch, "E361", {"start": v(-6.7, -31.4) * mm, "end": v(6.7, -31.4) * mm});
            skLineSegment(sketch, "E362.trimOffspring", {"start": v(6.7, -40.1) * mm, "end": v(6.7, -44.8) * mm});
            skLineSegment(sketch, "E363", {"start": v(-6.7, -31.4) * mm, "end": v(-6.7, -36.1) * mm});
            skLineSegment(sketch, "E364", {"start": v(-6.7, -40.1) * mm, "end": v(-6.7, -44.8) * mm});
            skLineSegment(sketch, "E365", {"start": v(6.7, -31.4) * mm, "end": v(6.7, -36.1) * mm});
            skLineSegment(sketch, "E366", {"start": v(-6.7, -44.8) * mm, "end": v(6.7, -44.8) * mm});
            skSolve(sketch);
        }
        {
            var Q0;
            Q0 = qSketchRegion(id + "F2", true);
            extrude(context, id + "F3", {"entities" : qUnion([Q0]), "operationType" : NewBodyOperationType.REMOVE, "endBound" : BoundingType.THROUGH_ALL, "oppositeDirection" : true, "depth" : 25 * mm});
        }
    });
